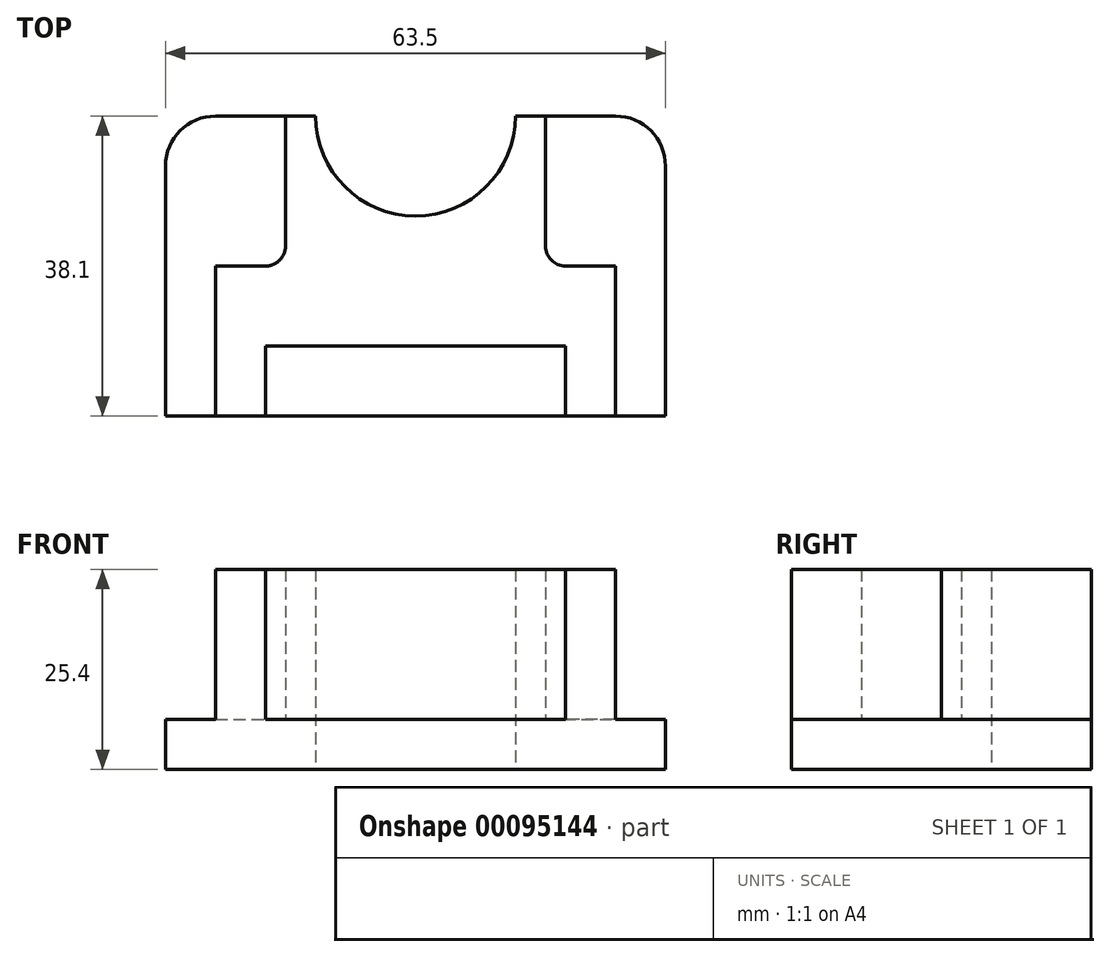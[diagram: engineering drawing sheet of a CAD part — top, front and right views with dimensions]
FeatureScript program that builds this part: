
annotation { "Feature Type Name" : "Feature", "Feature Type Description" : "" }
export const myFeature = defineFeature(function(context is Context, id is Id, definition is map)
    precondition{}
    {
        {
            var Q0;
            Q0=qCreatedBy(makeId("Top.planeOp"),FACE);
            var sketch = newSketch(context, id + "F0", { "sketchPlane" : qUnion([Q0])});
            skLineSegment(sketch, "E0.bottom", {"start": v(-24.1, 24.1) * mm, "end": v(-11.4, 24.1) * mm});
            skLineSegment(sketch, "E0.top", {"start": v(-30.44, -14) * mm, "end": v(33.06, -14) * mm});
            skLineSegment(sketch, "E0.left", {"start": v(-30.44, 17.75) * mm, "end": v(-30.44, -14) * mm});
            skLineSegment(sketch, "E0.right", {"start": v(33.06, 17.75) * mm, "end": v(33.06, -14) * mm});
            skPoint(sketch, "E1.visualSharp", {"position": v(-30.44, 24.1) * mm});
            skArc(sketch, "E1.filletArc", {"start": v(-24.1, 24.1) * mm, "mid": v(-28.58, 22.24) * mm, "end": v(-30.44, 17.75) * mm});
            skPoint(sketch, "E2.visualSharp", {"position": v(33.06, 24.1) * mm});
            skArc(sketch, "E2.filletArc", {"start": v(33.06, 17.75) * mm, "mid": v(31.2, 22.24) * mm, "end": v(26.7, 24.1) * mm});
            skArc(sketch, "E3", {"start": v(-11.4, 24.1) * mm, "mid": v(1.3, 11.4) * mm, "end": v(14, 24.1) * mm});
            skLineSegment(sketch, "E4.trimOffspring", {"start": v(14, 24.1) * mm, "end": v(26.7, 24.1) * mm});
            skSolve(sketch);
        }
        {
            var Q0;
            Q0=makeQuery(id+"F0.imprint","IMPRINT",FACE,{"disambiguationData":[TD([[makeQuery(id+"F0.imprint","IMPRINT",EDGE,{"derivedFrom":sQuery(id+"F0.wireOp",EDGE,"E0.bottom")}),-1.0]])]});
            extrude(context, id + "F1", {"entities" : qUnion([Q0]), "depth" : 6.35 * mm});
        }
        {
            var Q0;
            Q0=makeQuery(id+"F1.opExtrude","CAP_FACE",FACE,{"disambiguationData":[OSD([sQuery(id+"F0.wireOp",EDGE,"E0.bottom"),sQuery(id+"F0.wireOp",EDGE,"E0.top"),sQuery(id+"F0.wireOp",EDGE,"E0.left"),sQuery(id+"F0.wireOp",EDGE,"E0.right"),sQuery(id+"F0.wireOp",EDGE,"E1.filletArc"),sQuery(id+"F0.wireOp",EDGE,"E2.filletArc"),sQuery(id+"F0.wireOp",EDGE,"E3"),sQuery(id+"F0.wireOp",EDGE,"E4.trimOffspring")])],"isStart":false});
            var sketch = newSketch(context, id + "F2", { "sketchPlane" : qUnion([Q0])});
            skLineSegment(sketch, "E5.bottom", {"start": v(-24.1, -14) * mm, "end": v(-17.74, -14) * mm});
            skLineSegment(sketch, "E5.top", {"start": v(-24.1, 5.05) * mm, "end": v(-17.74, 5.05) * mm});
            skLineSegment(sketch, "E5.left", {"start": v(-24.1, -14) * mm, "end": v(-24.1, 5.05) * mm});
            skLineSegment(sketch, "E5.right", {"start": v(-17.74, -14) * mm, "end": v(-17.74, -5.11) * mm});
            skLineSegment(sketch, "E6.bottom", {"start": v(26.7, -14) * mm, "end": v(20.36, -14) * mm});
            skLineSegment(sketch, "E6.top", {"start": v(26.7, 5.05) * mm, "end": v(20.36, 5.05) * mm});
            skLineSegment(sketch, "E6.left", {"start": v(26.7, -14) * mm, "end": v(26.7, 5.05) * mm});
            skLineSegment(sketch, "E6.right", {"start": v(20.36, -14) * mm, "end": v(20.36, -5.11) * mm});
            skLineSegment(sketch, "E7", {"start": v(-17.74, -5.11) * mm, "end": v(20.36, -5.11) * mm});
            skArc(sketch, "E8", {"start": v(-11.4, 24.1) * mm, "mid": v(1.3, 11.41) * mm, "end": v(14, 24.1) * mm});
            skLineSegment(sketch, "E9", {"start": v(-11.4, 24.1) * mm, "end": v(-15.2, 24.1) * mm});
            skLineSegment(sketch, "E10", {"start": v(-15.2, 24.1) * mm, "end": v(-15.2, 7.55) * mm});
            skLineSegment(sketch, "E11", {"start": v(14, 24.1) * mm, "end": v(17.82, 24.1) * mm});
            skLineSegment(sketch, "E12", {"start": v(17.82, 24.1) * mm, "end": v(17.82, 7.59) * mm});
            skArc(sketch, "E13", {"start": v(-17.74, 5.05) * mm, "mid": v(-15.93, 5.8) * mm, "end": v(-15.2, 7.62) * mm});
            skArc(sketch, "E14", {"start": v(17.82, 7.59) * mm, "mid": v(18.56, 5.8) * mm, "end": v(20.36, 5.05) * mm});
            skSolve(sketch);
        }
        {
            var Q0;
            Q0=makeQuery(id+"F2.imprint","IMPRINT",FACE,{"disambiguationData":[TD([[makeQuery(id+"F2.imprint","IMPRINT",EDGE,{"derivedFrom":sQuery(id+"F2.wireOp",EDGE,"E5.bottom")}),1.0]])]});
            extrude(context, id + "F3", {"entities" : qUnion([Q0]), "operationType" : NewBodyOperationType.ADD, "depth" : 19.05 * mm});
        }
    });
